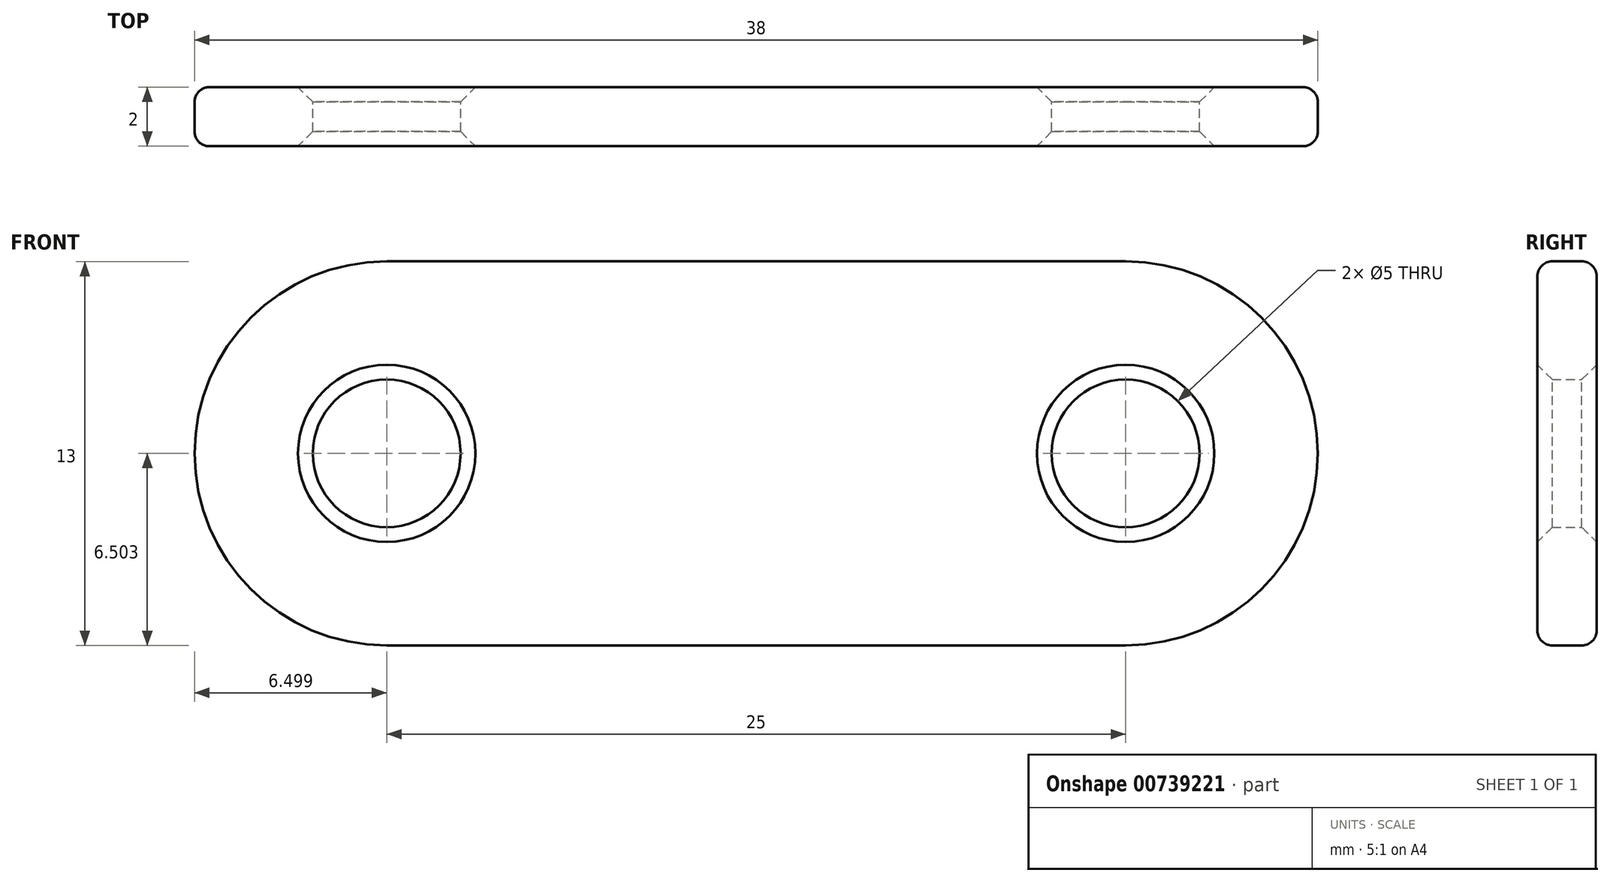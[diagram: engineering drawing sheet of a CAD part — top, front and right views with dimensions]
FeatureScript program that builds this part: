
annotation { "Feature Type Name" : "Feature", "Feature Type Description" : "" }
export const myFeature = defineFeature(function(context is Context, id is Id, definition is map)
    precondition{}
    {
        {
            var Q0;
            Q0=qCreatedBy(makeId("Front.planeOp"),FACE);
            var sketch = newSketch(context, id + "F0", { "sketchPlane" : qUnion([Q0])});
            skLineSegment(sketch, "E0", {"start": v(-17.93, 7.38) * mm, "end": v(7.07, 7.38) * mm});
            skLineSegment(sketch, "E1", {"start": v(-17.93, -5.62) * mm, "end": v(7.07, -5.62) * mm});
            skArc(sketch, "E2", {"start": v(-17.93, 7.38) * mm, "mid": v(-24.43, 0.88) * mm, "end": v(-17.93, -5.62) * mm});
            skArc(sketch, "E3", {"start": v(7.07, -5.62) * mm, "mid": v(13.57, 0.88) * mm, "end": v(7.07, 7.38) * mm});
            skCircle(sketch, "E4", {"center": v(-17.93, 0.88) * mm, "radius": 2.5 * mm});
            skCircle(sketch, "E5", {"center": v(7.07, 0.88) * mm, "radius": 2.5 * mm});
            skSolve(sketch);
        }
        {
            var Q0;
            Q0 = qSketchRegion(id + "F0", true);
            extrude(context, id + "F1", {"entities" : qUnion([Q0]), "depth" : 2 * mm, "offsetDistance" : 25.4 * mm});
        }
        {
            var Q0;
            Q0=makeQuery(id+"F1.opExtrude","CAP_EDGE",EDGE,{"disambiguationData":[OSD([sQuery(id+"F0.wireOp",EDGE,"E0")])],"isStart":false});
            var Q1;
            Q1=makeQuery(id+"F1.opExtrude","CAP_EDGE",EDGE,{"disambiguationData":[OSD([sQuery(id+"F0.wireOp",EDGE,"E2")])],"isStart":true});
            fillet(context, id + "F2", {"entities" : qUnion([Q0, Q1]), "radius" : 0.5 * mm, "tangentPropagation" : true, "allowEdgeOverflow" : false});
        }
        {
            var Q0;
            Q0=makeQuery(id+"F1.opExtrude","CAP_EDGE",EDGE,{"disambiguationData":[OSD([sQuery(id+"F0.wireOp",EDGE,"E4")])],"isStart":true});
            var Q1;
            Q1=makeQuery(id+"F1.opExtrude","CAP_EDGE",EDGE,{"disambiguationData":[OSD([sQuery(id+"F0.wireOp",EDGE,"E5")])],"isStart":true});
            var Q2;
            Q2=makeQuery(id+"F1.opExtrude","CAP_EDGE",EDGE,{"disambiguationData":[OSD([sQuery(id+"F0.wireOp",EDGE,"E4")])],"isStart":false});
            var Q3;
            Q3=makeQuery(id+"F1.opExtrude","CAP_EDGE",EDGE,{"disambiguationData":[OSD([sQuery(id+"F0.wireOp",EDGE,"E5")])],"isStart":false});
            chamfer(context, id + "F3", {"entities" : qUnion([Q0, Q1, Q2, Q3]), "width" : 0.5 * mm, "tangentPropagation" : true});
        }
    });
